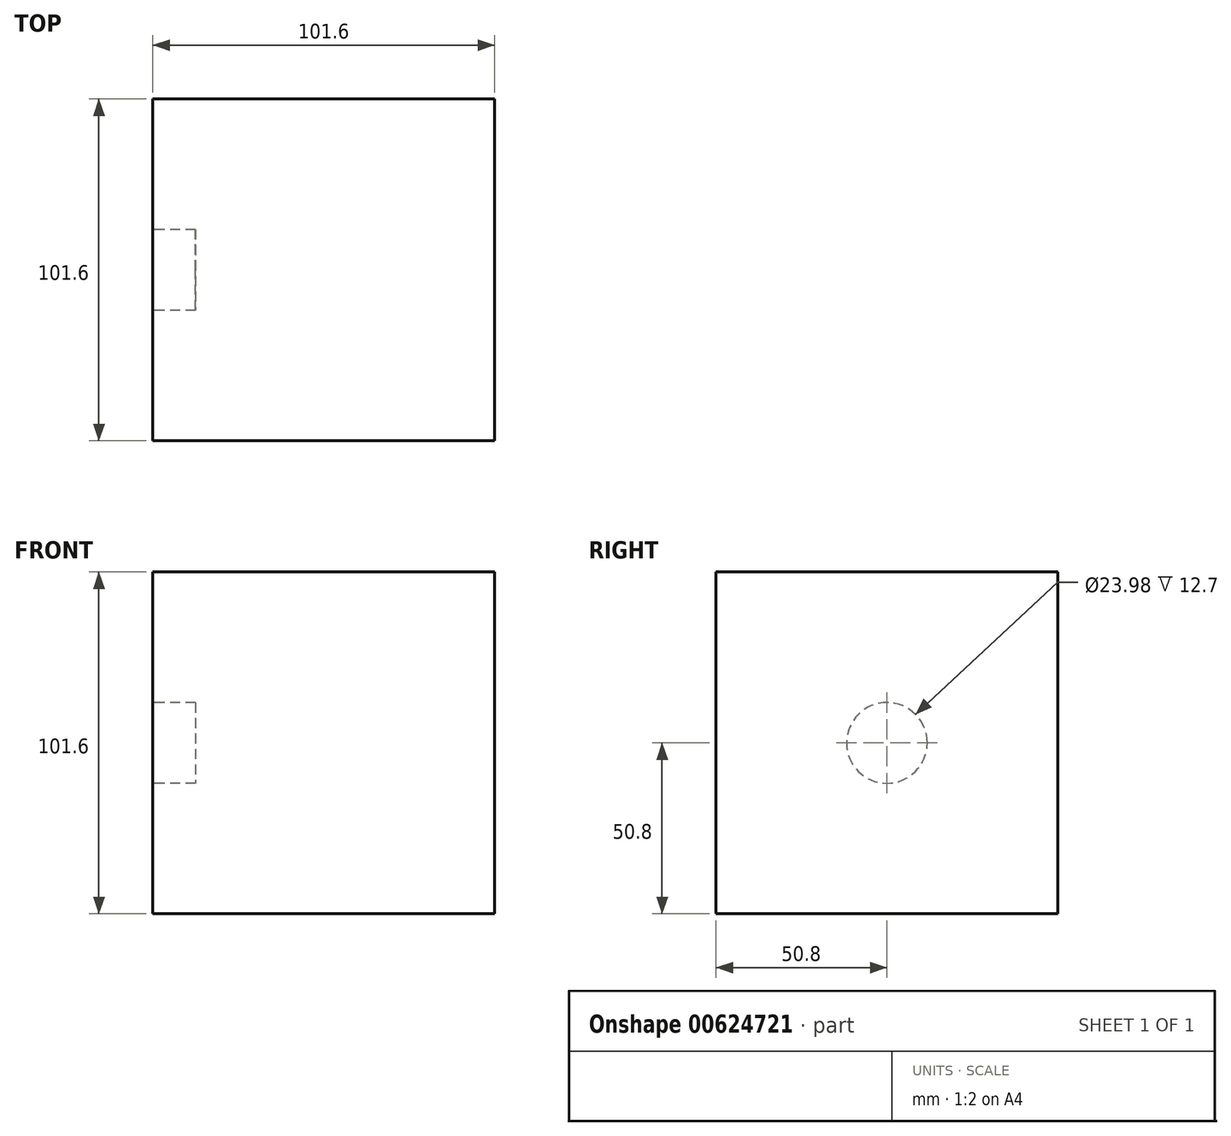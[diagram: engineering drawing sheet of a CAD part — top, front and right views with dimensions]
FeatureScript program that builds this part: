
annotation { "Feature Type Name" : "Feature", "Feature Type Description" : "" }
export const myFeature = defineFeature(function(context is Context, id is Id, definition is map)
    precondition{}
    {
        {
            var Q0;
            Q0=qCreatedBy(makeId("Top.planeOp"),FACE);
            var sketch = newSketch(context, id + "F0", { "sketchPlane" : qUnion([Q0])});
            skLineSegment(sketch, "E0.bottom", {"start": v(-50.8, 50.8) * mm, "end": v(50.8, 50.8) * mm});
            skLineSegment(sketch, "E0.top", {"start": v(-50.8, -50.8) * mm, "end": v(50.8, -50.8) * mm});
            skLineSegment(sketch, "E0.left", {"start": v(-50.8, 50.8) * mm, "end": v(-50.8, -50.8) * mm});
            skLineSegment(sketch, "E0.right", {"start": v(50.8, 50.8) * mm, "end": v(50.8, -50.8) * mm});
            skSolve(sketch);
        }
        {
            var Q0;
            Q0 = qSketchRegion(id + "F0", true);
            extrude(context, id + "F1", {"entities" : qUnion([Q0]), "depth" : 50.8 * mm, "offsetDistance" : 25.4 * mm, "hasSecondDirection" : true, "secondDirectionOppositeDirection" : true, "secondDirectionDepth" : 50.8 * mm});
        }
        {
            var Q0;
            Q0=makeQuery(id+"F1.opExtrude","SWEPT_FACE",FACE,{"disambiguationData":[OSD([sQuery(id+"F0.wireOp",EDGE,"E0.left")])]});
            var sketch = newSketch(context, id + "F2", { "sketchPlane" : qUnion([Q0])});
            skCircle(sketch, "E1", {"center": v(0, 0) * mm, "radius": 11.99 * mm});
            skSolve(sketch);
        }
        {
            var Q0;
            Q0=makeQuery(id+"F2.imprint","IMPRINT",FACE,{"disambiguationData":[TD([[makeQuery(id+"F2.imprint","IMPRINT",EDGE,{"derivedFrom":sQuery(id+"F2.wireOp",EDGE,"E1")}),1.0]])]});
            extrude(context, id + "F3", {"entities" : qUnion([Q0]), "operationType" : NewBodyOperationType.REMOVE, "oppositeDirection" : true, "depth" : 12.7 * mm, "offsetDistance" : 25.4 * mm});
        }
    });
